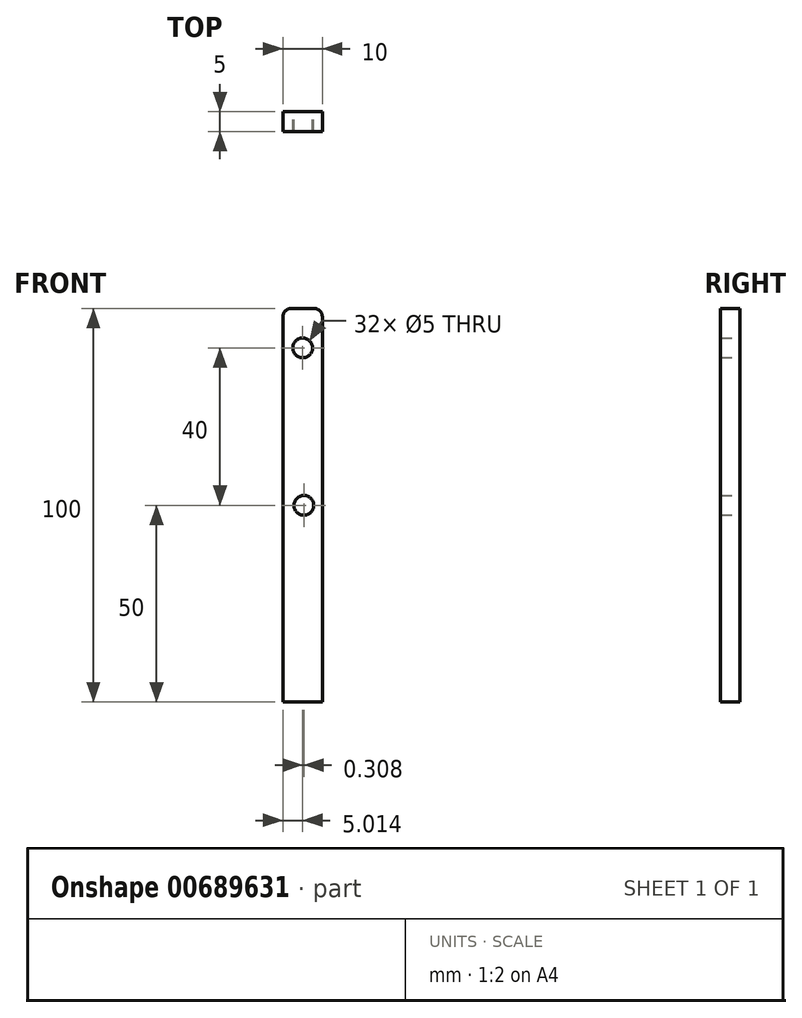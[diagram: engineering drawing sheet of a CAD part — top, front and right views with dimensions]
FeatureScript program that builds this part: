
annotation { "Feature Type Name" : "Feature", "Feature Type Description" : "" }
export const myFeature = defineFeature(function(context is Context, id is Id, definition is map)
    precondition{}
    {
        {
            var Q0;
            Q0=qCreatedBy(makeId("Front.planeOp"),FACE);
            var sketch = newSketch(context, id + "F0", { "sketchPlane" : qUnion([Q0])});
            skLineSegment(sketch, "E0", {"start": v(0, 0) * mm, "end": v(-10, 0) * mm});
            skLineSegment(sketch, "E1", {"start": v(-10, 0) * mm, "end": v(-10, 98) * mm});
            skLineSegment(sketch, "E2", {"start": v(-8, 100) * mm, "end": v(-2, 100) * mm});
            skLineSegment(sketch, "E3", {"start": v(0, 98) * mm, "end": v(0, 0) * mm});
            skCircle(sketch, "E4", {"center": v(-4.68, 50) * mm, "radius": 2.5 * mm});
            skCircle(sketch, "E5", {"center": v(-4.99, 90) * mm, "radius": 2.5 * mm});
            skPoint(sketch, "E6.visualSharp", {"position": v(-10, 100) * mm});
            skArc(sketch, "E6.filletArc", {"start": v(-8, 100) * mm, "mid": v(-9.41, 99.41) * mm, "end": v(-10, 98) * mm});
            skPoint(sketch, "E7.visualSharp", {"position": v(0, 100) * mm});
            skArc(sketch, "E7.filletArc", {"start": v(0, 98) * mm, "mid": v(-0.59, 99.41) * mm, "end": v(-2, 100) * mm});
            skSolve(sketch);
        }
        {
            var Q0;
            Q0=makeQuery(id+"F0.imprint","IMPRINT",FACE,{"disambiguationData":[TD([[makeQuery(id+"F0.imprint","IMPRINT",EDGE,{"derivedFrom":sQuery(id+"F0.wireOp",EDGE,"E0")}),-1.0]])]});
            extrude(context, id + "F1", {"entities" : qUnion([Q0]), "depth" : 5 * mm, "offsetDistance" : 25 * mm});
        }
    });
